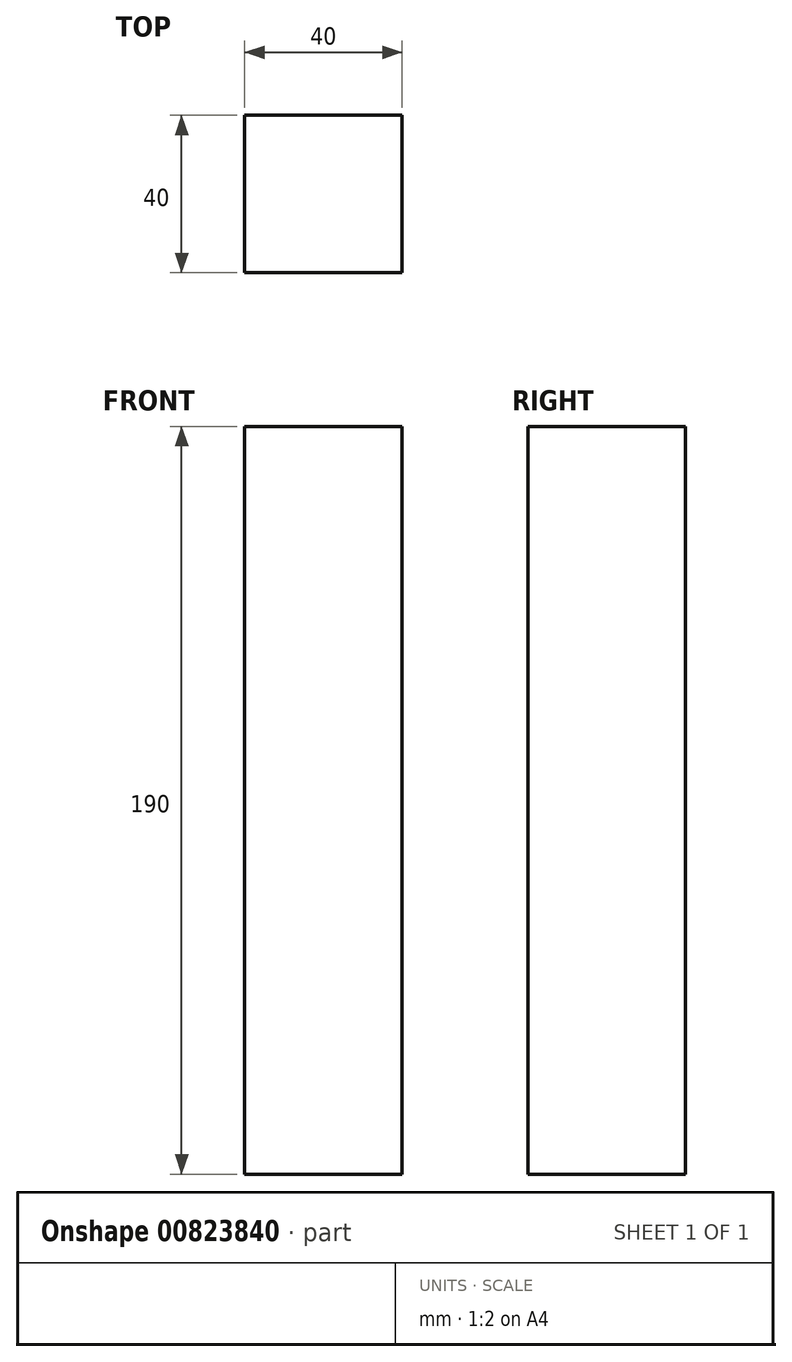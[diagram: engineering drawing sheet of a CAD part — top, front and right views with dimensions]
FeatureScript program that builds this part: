
annotation { "Feature Type Name" : "Feature", "Feature Type Description" : "" }
export const myFeature = defineFeature(function(context is Context, id is Id, definition is map)
    precondition{}
    {
        {
            var Q0;
            Q0=qCreatedBy(makeId("Top.planeOp"),FACE);
            var sketch = newSketch(context, id + "F0", { "sketchPlane" : qUnion([Q0])});
            skLineSegment(sketch, "E0.bottom", {"start": v(20, -20) * mm, "end": v(-20, -20) * mm});
            skLineSegment(sketch, "E0.top", {"start": v(20, 20) * mm, "end": v(-20, 20) * mm});
            skLineSegment(sketch, "E0.left", {"start": v(20, -20) * mm, "end": v(20, 20) * mm});
            skLineSegment(sketch, "E0.right", {"start": v(-20, -20) * mm, "end": v(-20, 20) * mm});
            skPoint(sketch, "E0.middle", {"position": v(0, 0) * mm});
            skSolve(sketch);
        }
        {
            var Q0;
            Q0 = qSketchRegion(id + "F0", true);
            extrude(context, id + "F1", {"entities" : qUnion([Q0]), "depth" : 190 * mm, "offsetDistance" : 25 * mm});
        }
    });
